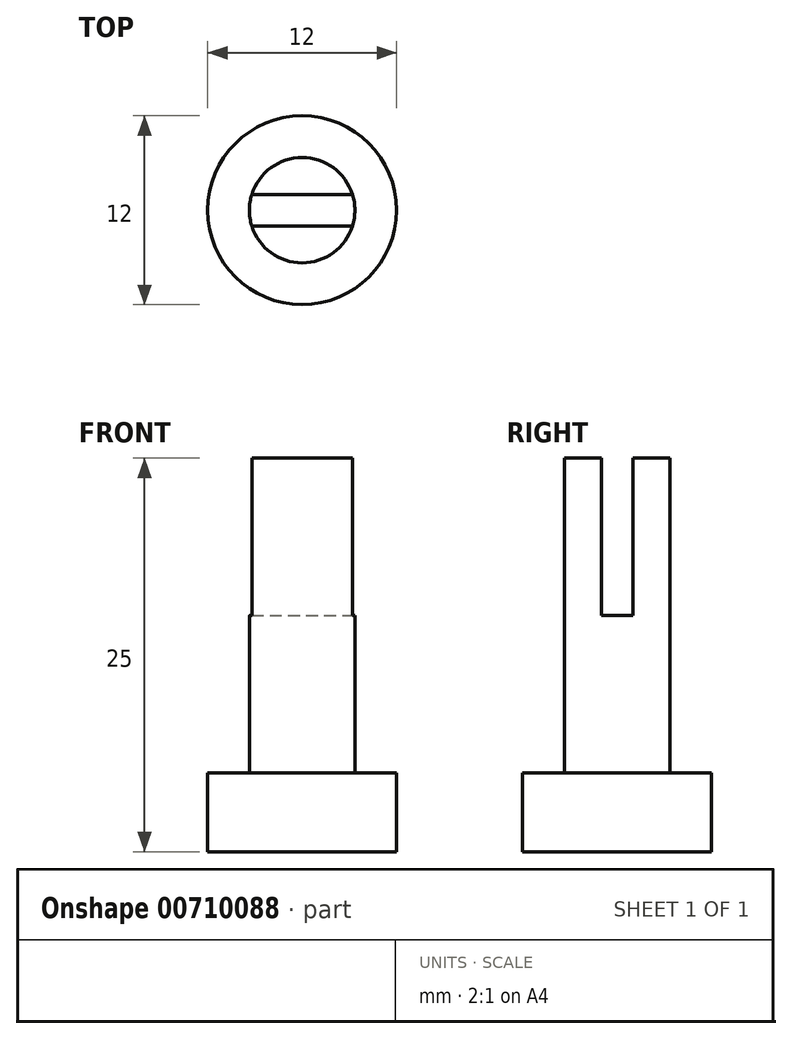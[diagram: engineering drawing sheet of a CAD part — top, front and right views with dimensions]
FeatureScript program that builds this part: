
annotation { "Feature Type Name" : "Feature", "Feature Type Description" : "" }
export const myFeature = defineFeature(function(context is Context, id is Id, definition is map)
    precondition{}
    {
        {
            var Q0;
            Q0=qCreatedBy(makeId("Top.planeOp"),FACE);
            var sketch = newSketch(context, id + "F0", { "sketchPlane" : qUnion([Q0])});
            skCircle(sketch, "E0", {"center": v(0, 0) * mm, "radius": 6 * mm});
            skCircle(sketch, "E1", {"center": v(0, 0) * mm, "radius": 3.35 * mm});
            skSolve(sketch);
        }
        {
            var Q0;
            Q0=makeQuery(id+"F0.imprint","IMPRINT",FACE,{"disambiguationData":[TD([[makeQuery(id+"F0.imprint","IMPRINT",EDGE,{"derivedFrom":sQuery(id+"F0.wireOp",EDGE,"E1")}),1.0]])]});
            extrude(context, id + "F1", {"entities" : qUnion([Q0]), "depth" : 25 * mm, "offsetDistance" : 25 * mm});
        }
        {
            var Q0;
            Q0=makeQuery(id+"F0.imprint","IMPRINT",FACE,{"disambiguationData":[TD([[makeQuery(id+"F0.imprint","IMPRINT",EDGE,{"derivedFrom":sQuery(id+"F0.wireOp",EDGE,"E0")}),1.0]])]});
            extrude(context, id + "F2", {"entities" : qUnion([Q0]), "operationType" : NewBodyOperationType.ADD, "depth" : 5 * mm, "offsetDistance" : 25 * mm});
        }
        {
            var Q0;
            Q0=makeQuery(id+"F1.opExtrude","CAP_FACE",FACE,{"disambiguationData":[OSD([sQuery(id+"F0.wireOp",EDGE,"E1")])],"isStart":false});
            var sketch = newSketch(context, id + "F3", { "sketchPlane" : qUnion([Q0])});
            skLineSegment(sketch, "E2", {"start": v(-3.2, -1) * mm, "end": v(3.2, -1) * mm});
            skLineSegment(sketch, "E3", {"start": v(-3.2, 1) * mm, "end": v(3.2, 1) * mm});
            skSolve(sketch);
        }
        {
            var Q0;
            {var subQ0=sQuery(id+"F3.wireOp",EDGE,"E2");Q0=makeQuery(id+"F3.imprint","IMPRINT",FACE,{"disambiguationData":[TD([[makeQuery(id+"F3.imprint","IMPRINT",EDGE,{"derivedFrom":subQ0}),1.0]])]});}
            extrude(context, id + "F4", {"entities" : qUnion([Q0]), "operationType" : NewBodyOperationType.REMOVE, "oppositeDirection" : true, "depth" : 10 * mm, "offsetDistance" : 25 * mm});
        }
    });
